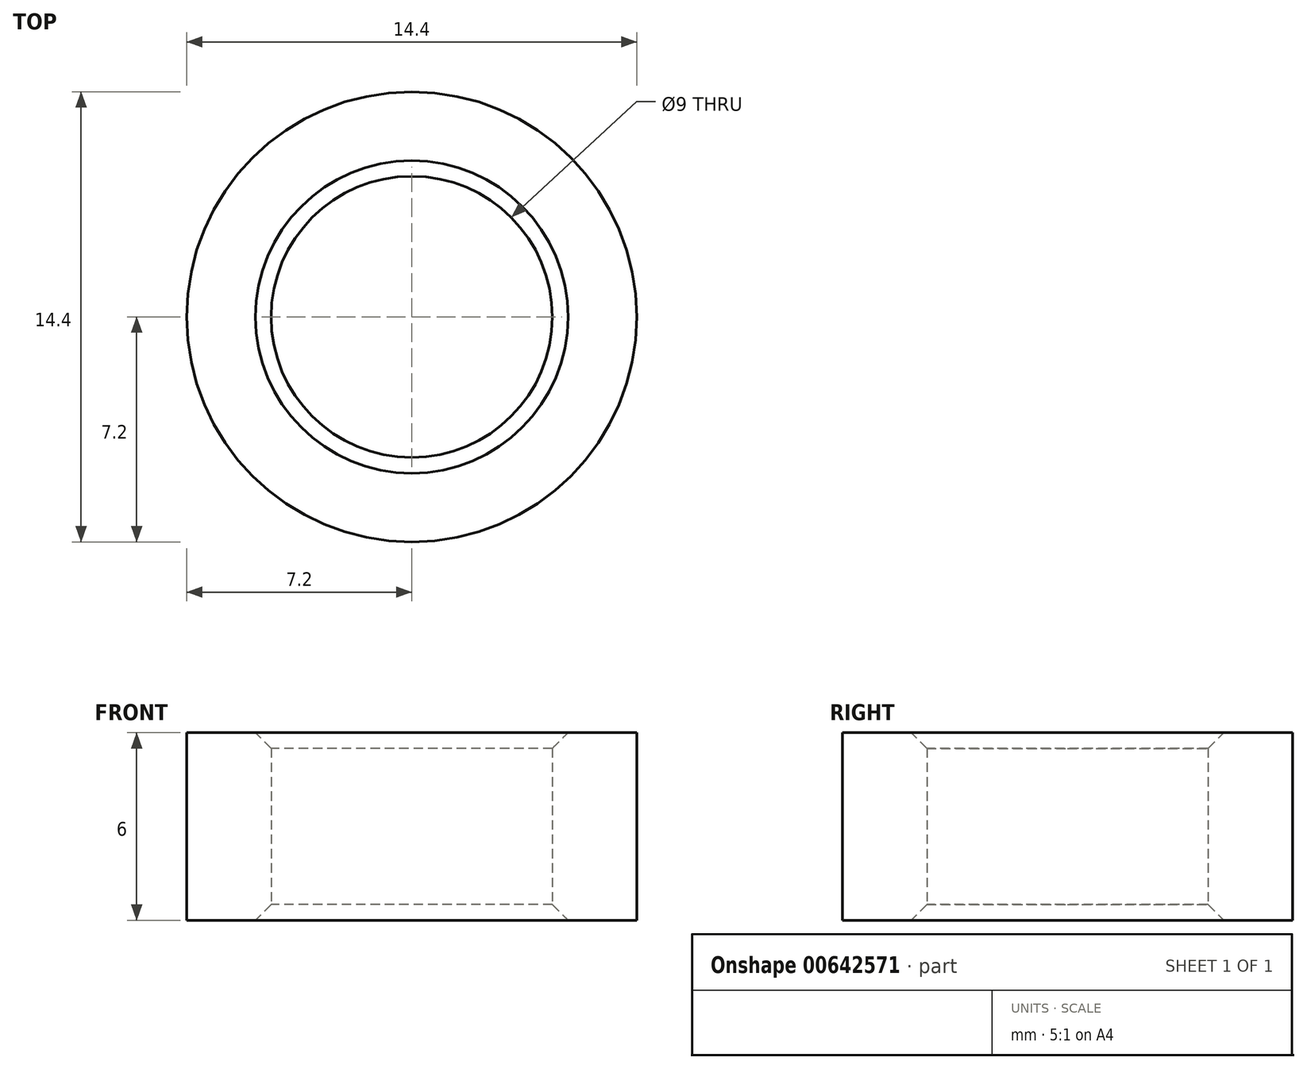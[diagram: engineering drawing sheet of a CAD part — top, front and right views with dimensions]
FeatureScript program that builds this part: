
annotation { "Feature Type Name" : "Feature", "Feature Type Description" : "" }
export const myFeature = defineFeature(function(context is Context, id is Id, definition is map)
    precondition{}
    {
        {
            var Q0;
            Q0=qCreatedBy(makeId("Top.planeOp"),FACE);
            var sketch = newSketch(context, id + "F0", { "sketchPlane" : qUnion([Q0])});
            skCircle(sketch, "E0", {"center": v(0, 0) * mm, "radius": 7.2 * mm});
            skCircle(sketch, "E1", {"center": v(0, 0) * mm, "radius": 4.5 * mm});
            skSolve(sketch);
        }
        {
            var Q0;
            Q0=sQuery(id+"F0.wireOp",EDGE,"E0");
            extrude(context, id + "F1", {"bodyType" : ToolBodyType.SURFACE, "surfaceEntities" : qUnion([Q0]), "depth" : 6 * mm, "offsetDistance" : 25 * mm});
        }
        {
            var Q0;
            Q0 = qSketchRegion(id + "F0", true);
            extrude(context, id + "F2", {"entities" : qUnion([Q0]), "depth" : 6 * mm, "offsetDistance" : 25 * mm});
        }
        {
            var Q0;
            Q0=makeQuery(id+"F2.opExtrude","CAP_EDGE",EDGE,{"disambiguationData":[OSD([sQuery(id+"F0.wireOp",EDGE,"E1")])],"isStart":true});
            chamfer(context, id + "F3", {"entities" : qUnion([Q0]), "chamferType" : ChamferType.OFFSET_ANGLE, "width" : 0.5 * mm, "oppositeDirection" : false, "angle" : 45 * degree, "tangentPropagation" : true});
        }
        {
            var Q0;
            Q0=makeQuery(id+"F2.opExtrude","CAP_EDGE",EDGE,{"disambiguationData":[OSD([sQuery(id+"F0.wireOp",EDGE,"E1")])],"isStart":false});
            chamfer(context, id + "F4", {"entities" : qUnion([Q0]), "chamferType" : ChamferType.OFFSET_ANGLE, "width" : 0.5 * mm, "oppositeDirection" : false, "angle" : 45 * degree, "tangentPropagation" : true});
        }
    });
